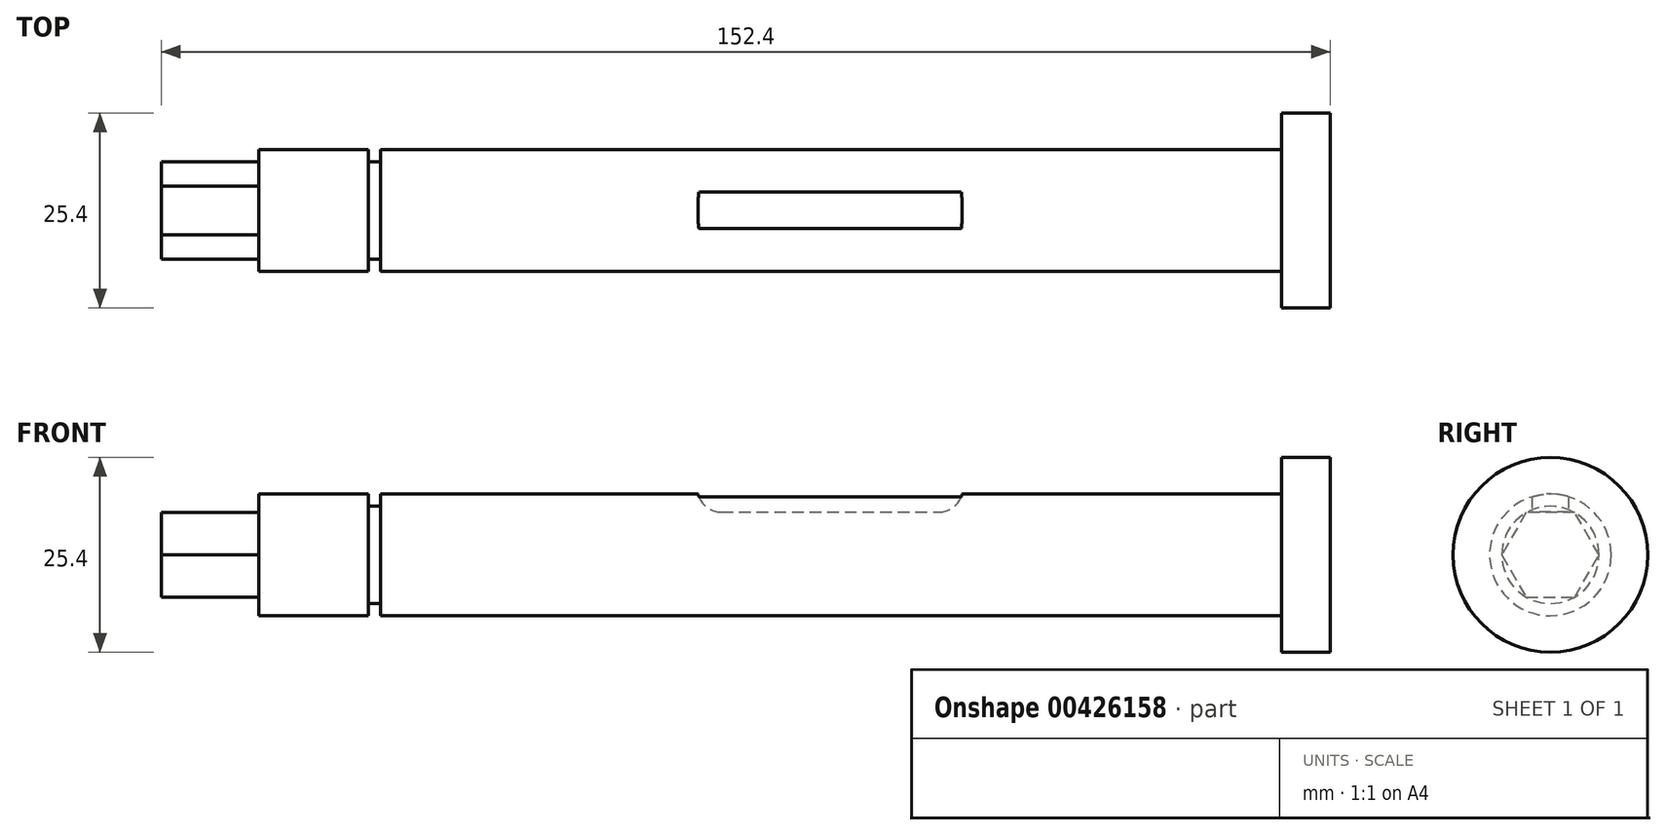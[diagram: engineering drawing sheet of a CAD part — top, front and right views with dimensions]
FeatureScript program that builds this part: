
annotation { "Feature Type Name" : "Feature", "Feature Type Description" : "" }
export const myFeature = defineFeature(function(context is Context, id is Id, definition is map)
    precondition{}
    {
        {
            var Q0;
            Q0=qCreatedBy(makeId("Front.planeOp"),FACE);
            var sketch = newSketch(context, id + "F0", { "sketchPlane" : qUnion([Q0])});
            skLineSegment(sketch, "E0", {"start": v(0, 6.35) * mm, "end": v(12.7, 6.35) * mm});
            skLineSegment(sketch, "E1", {"start": v(12.7, 6.35) * mm, "end": v(12.7, 7.94) * mm});
            skLineSegment(sketch, "E2", {"start": v(12.7, 7.94) * mm, "end": v(26.97, 7.94) * mm});
            skLineSegment(sketch, "E3", {"start": v(26.97, 7.94) * mm, "end": v(26.97, 6.34) * mm});
            skLineSegment(sketch, "E4", {"start": v(26.97, 6.34) * mm, "end": v(28.58, 6.34) * mm});
            skLineSegment(sketch, "E5", {"start": v(28.58, 6.34) * mm, "end": v(28.58, 7.94) * mm});
            skLineSegment(sketch, "E6", {"start": v(28.58, 7.94) * mm, "end": v(146.05, 7.94) * mm});
            skLineSegment(sketch, "E7", {"start": v(146.05, 7.94) * mm, "end": v(146.05, 12.7) * mm});
            skLineSegment(sketch, "E8", {"start": v(146.05, 12.7) * mm, "end": v(152.4, 12.7) * mm});
            skLineSegment(sketch, "E9", {"start": v(152.4, 12.7) * mm, "end": v(152.4, 0) * mm});
            skLineSegment(sketch, "E10", {"start": v(0, 6.35) * mm, "end": v(0, 0) * mm});
            skLineSegment(sketch, "E11", {"start": v(0, 0) * mm, "end": v(152.4, 0) * mm});
            skSolve(sketch);
        }
        {
            var Q0;
            Q0 = qSketchRegion(id + "F0", true);
            var Q1;
            Q1=sQuery(id+"F0.wireOp",EDGE,"E11");
            revolve(context, id + "F1", {"surfaceOperationType" : NewSurfaceOperationType.NEW, "entities" : qUnion([Q0]), "axis" : qUnion([Q1]), "revolveType" : RevolveType.FULL});
        }
        {
            var Q0;
            Q0=qCreatedBy(makeId("Front.planeOp"),FACE);
            var sketch = newSketch(context, id + "F2", { "sketchPlane" : qUnion([Q0])});
            skLineSegment(sketch, "E12", {"start": v(69.85, 15.1) * mm, "end": v(69.85, 8.74) * mm});
            skLineSegment(sketch, "E13", {"start": v(73.02, 5.57) * mm, "end": v(101.35, 5.57) * mm});
            skLineSegment(sketch, "E14", {"start": v(104.52, 8.74) * mm, "end": v(104.52, 15.1) * mm});
            skLineSegment(sketch, "E15", {"start": v(104.52, 15.1) * mm, "end": v(69.85, 15.1) * mm});
            skPoint(sketch, "E16.visualSharp", {"position": v(69.85, 5.57) * mm});
            skArc(sketch, "E16.filletArc", {"start": v(69.85, 8.74) * mm, "mid": v(70.78, 6.5) * mm, "end": v(73.02, 5.57) * mm});
            skPoint(sketch, "E17.visualSharp", {"position": v(104.52, 5.57) * mm});
            skArc(sketch, "E17.filletArc", {"start": v(101.35, 5.57) * mm, "mid": v(103.6, 6.5) * mm, "end": v(104.52, 8.74) * mm});
            skSolve(sketch);
        }
        {
            var Q0;
            Q0 = qSketchRegion(id + "F2", true);
            extrude(context, id + "F3", {"entities" : qUnion([Q0]), "operationType" : NewBodyOperationType.REMOVE, "oppositeDirection" : true, "depth" : 2.38 * mm, "offsetDistance" : 25.4 * mm, "hasSecondDirection" : true, "secondDirectionOppositeDirection" : false, "secondDirectionDepth" : 2.38 * mm});
        }
        {
            var Q0;
            Q0=makeQuery(id+"F1.opRevolve","SWEPT_FACE",FACE,{"disambiguationData":[OSD([sQuery(id+"F0.wireOp",EDGE,"E10")])]});
            var sketch = newSketch(context, id + "F4", { "sketchPlane" : qUnion([Q0])});
            skCircle(sketch, "E18.cCircle", {"center": v(0, 0) * mm, "radius": 6.35 * mm, "construction": true});
            skLineSegment(sketch, "E18.0", {"start": v(-3.18, 5.5) * mm, "end": v(3.17, 5.5) * mm});
            skLineSegment(sketch, "E18.1", {"start": v(3.17, 5.5) * mm, "end": v(6.35, 0) * mm});
            skLineSegment(sketch, "E18.2", {"start": v(6.35, 0) * mm, "end": v(3.18, -5.5) * mm});
            skLineSegment(sketch, "E18.3", {"start": v(3.18, -5.5) * mm, "end": v(-3.17, -5.5) * mm});
            skLineSegment(sketch, "E18.4", {"start": v(-3.17, -5.5) * mm, "end": v(-6.35, 0) * mm});
            skLineSegment(sketch, "E18.5", {"start": v(-6.35, 0) * mm, "end": v(-3.17, 5.5) * mm});
            skSolve(sketch);
        }
        {
            var Q0;
            {var subQ0=sQuery(id+"F4.wireOp",EDGE,"E18.5");Q0=makeQuery(id+"F4.imprint","IMPRINT",FACE,{"disambiguationData":[TD([[makeQuery(id+"F4.imprint","IMPRINT",EDGE,{"derivedFrom":subQ0}),1.0]])]});}
            var Q1;
            {var subQ0=sQuery(id+"F4.wireOp",EDGE,"E18.0");Q1=makeQuery(id+"F4.imprint","IMPRINT",FACE,{"disambiguationData":[TD([[makeQuery(id+"F4.imprint","IMPRINT",EDGE,{"derivedFrom":subQ0}),1.0]])]});}
            var Q2;
            {var subQ0=sQuery(id+"F4.wireOp",EDGE,"E18.1");Q2=makeQuery(id+"F4.imprint","IMPRINT",FACE,{"disambiguationData":[TD([[makeQuery(id+"F4.imprint","IMPRINT",EDGE,{"derivedFrom":subQ0}),1.0]])]});}
            var Q3;
            {var subQ0=sQuery(id+"F4.wireOp",EDGE,"E18.2");Q3=makeQuery(id+"F4.imprint","IMPRINT",FACE,{"disambiguationData":[TD([[makeQuery(id+"F4.imprint","IMPRINT",EDGE,{"derivedFrom":subQ0}),1.0]])]});}
            var Q4;
            {var subQ0=sQuery(id+"F4.wireOp",EDGE,"E18.3");Q4=makeQuery(id+"F4.imprint","IMPRINT",FACE,{"disambiguationData":[TD([[makeQuery(id+"F4.imprint","IMPRINT",EDGE,{"derivedFrom":subQ0}),1.0]])]});}
            var Q5;
            {var subQ0=sQuery(id+"F4.wireOp",EDGE,"E18.4");Q5=makeQuery(id+"F4.imprint","IMPRINT",FACE,{"disambiguationData":[TD([[makeQuery(id+"F4.imprint","IMPRINT",EDGE,{"derivedFrom":subQ0}),1.0]])]});}
            var Q6;
            Q6=makeQuery(id+"F1.opRevolve","SWEPT_FACE",FACE,{"disambiguationData":[OSD([sQuery(id+"F0.wireOp",EDGE,"E1")])]});
            extrude(context, id + "F5", {"entities" : qUnion([Q0, Q1, Q2, Q3, Q4, Q5]), "operationType" : NewBodyOperationType.REMOVE, "endBound" : BoundingType.UP_TO_SURFACE, "oppositeDirection" : true, "depth" : 25.4 * mm, "endBoundEntityFace" : qUnion([Q6]), "offsetDistance" : 25.4 * mm});
        }
    });
